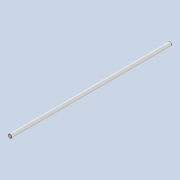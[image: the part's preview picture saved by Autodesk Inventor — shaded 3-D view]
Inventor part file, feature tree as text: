
AUTODESK INVENTOR PART (.ipt)
format: ipt  version: 2020 (Build 240168000, 168)  size: 76,800 bytes
history: native  units: mm
features: extrude x1, chamfer x1, sketch x1
ambient origin geometry x8: Origin, YZ Plane, XZ Plane, XY Plane, X Axis, Y Axis, Z Axis, Center Point
bodies: Solid1 (feature_tree)
feature tree (3):
  extrude  "Extrusion1"  Depth=442.0mm TaperAngle=0.0deg
  chamfer  "Chamfer1"  Distance=0.5mm Angle=45.0deg
  sketch  "Sketch1"  dims[d0=10.0mm d1=442.0mm d2=0.0mm d3=0.5mm d4=2.0mm d5=45.0deg]
